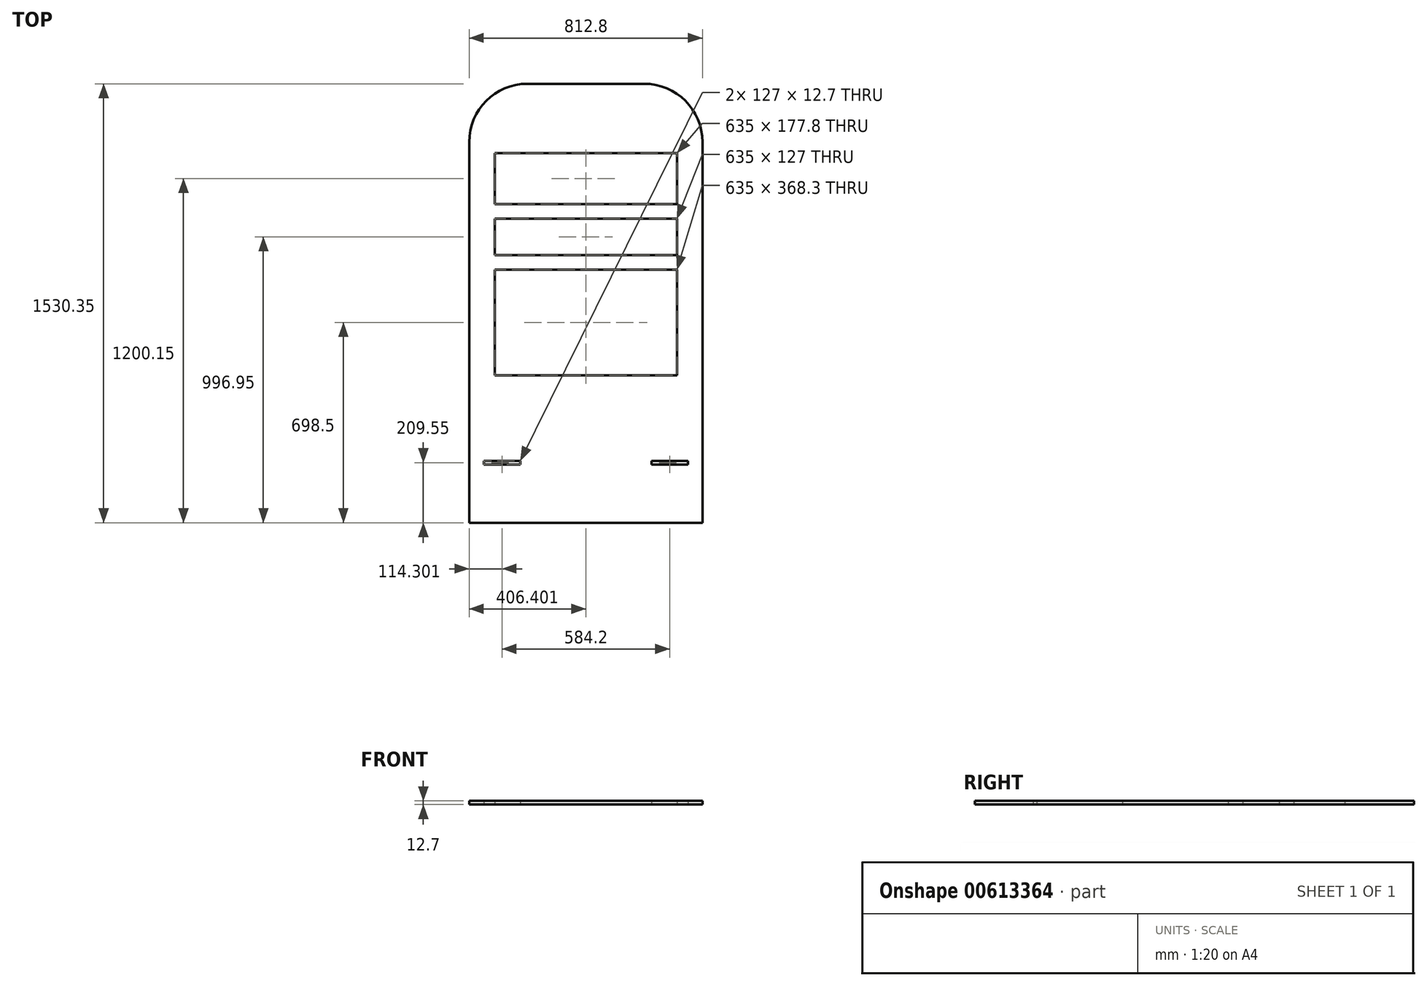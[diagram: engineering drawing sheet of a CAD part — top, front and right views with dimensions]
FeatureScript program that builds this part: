
annotation { "Feature Type Name" : "Feature", "Feature Type Description" : "" }
export const myFeature = defineFeature(function(context is Context, id is Id, definition is map)
    precondition{}
    {
        {
            var Q0;
            Q0=qCreatedBy(makeId("Top.planeOp"),FACE);
            var sketch = newSketch(context, id + "F0", { "sketchPlane" : qUnion([Q0])});
            skLineSegment(sketch, "E0.left", {"start": v(-648.04, 763.82) * mm, "end": v(-648.04, -556.98) * mm});
            skLineSegment(sketch, "E0.right", {"start": v(164.76, 763.82) * mm, "end": v(164.76, -556.98) * mm});
            skLineSegment(sketch, "E1.0", {"start": v(-559.14, -48.98) * mm, "end": v(75.86, -48.98) * mm});
            skLineSegment(sketch, "E2.0", {"start": v(-559.14, 725.72) * mm, "end": v(-559.14, 547.92) * mm});
            skLineSegment(sketch, "E3.0", {"start": v(-559.14, 725.72) * mm, "end": v(75.86, 725.72) * mm});
            skLineSegment(sketch, "E4.0", {"start": v(75.86, 725.72) * mm, "end": v(75.86, 547.92) * mm});
            skLineSegment(sketch, "E5.0", {"start": v(-559.14, 319.32) * mm, "end": v(75.86, 319.32) * mm});
            skLineSegment(sketch, "E6.trimOffspring", {"start": v(-559.14, 90.72) * mm, "end": v(-559.14, -48.98) * mm});
            skLineSegment(sketch, "E7.trimOffspring", {"start": v(75.86, 90.72) * mm, "end": v(75.86, -48.98) * mm});
            skLineSegment(sketch, "E8.trimOffspring", {"start": v(75.86, 319.32) * mm, "end": v(75.86, 141.52) * mm});
            skLineSegment(sketch, "E9.trimOffspring", {"start": v(-559.14, 319.32) * mm, "end": v(-559.14, 141.52) * mm});
            skLineSegment(sketch, "E10.trimOffspring", {"start": v(-559.14, 497.12) * mm, "end": v(-559.14, 370.12) * mm});
            skLineSegment(sketch, "E11.trimOffspring", {"start": v(75.86, 497.12) * mm, "end": v(75.86, 370.12) * mm});
            skLineSegment(sketch, "E12", {"start": v(-559.14, 370.12) * mm, "end": v(75.86, 370.12) * mm});
            skLineSegment(sketch, "E13", {"start": v(-559.14, 90.72) * mm, "end": v(-559.14, 141.52) * mm});
            skLineSegment(sketch, "E14", {"start": v(75.86, 90.72) * mm, "end": v(75.86, 141.52) * mm});
            skLineSegment(sketch, "E15", {"start": v(-559.14, 547.92) * mm, "end": v(75.86, 547.92) * mm});
            skLineSegment(sketch, "E16", {"start": v(75.86, 497.12) * mm, "end": v(-559.14, 497.12) * mm});
            skLineSegment(sketch, "E17", {"start": v(-444.84, 967.02) * mm, "end": v(-38.44, 967.02) * mm});
            skPoint(sketch, "E18.visualSharp", {"position": v(-648.04, 967.02) * mm});
            skArc(sketch, "E18.filletArc", {"start": v(-444.84, 967.02) * mm, "mid": v(-588.52, 907.5) * mm, "end": v(-648.04, 763.82) * mm});
            skPoint(sketch, "E19.visualSharp", {"position": v(164.76, 967.02) * mm});
            skArc(sketch, "E19.filletArc", {"start": v(164.76, 763.82) * mm, "mid": v(105.25, 907.5) * mm, "end": v(-38.44, 967.02) * mm});
            skLineSegment(sketch, "E20.0", {"start": v(-648.04, -563.33) * mm, "end": v(164.76, -563.33) * mm});
            skLineSegment(sketch, "E21", {"start": v(-648.04, -556.98) * mm, "end": v(-648.04, -563.33) * mm});
            skLineSegment(sketch, "E22", {"start": v(164.76, -556.98) * mm, "end": v(164.76, -563.33) * mm});
            skLineSegment(sketch, "E23.MirrorCS", {"start": v(-597.24, -360.13) * mm, "end": v(-597.24, -347.43) * mm});
            skLineSegment(sketch, "E24.MirrorCS", {"start": v(-470.24, -360.13) * mm, "end": v(-470.24, -347.43) * mm});
            skLineSegment(sketch, "E25.MirrorCS", {"start": v(113.96, -360.13) * mm, "end": v(113.96, -347.43) * mm});
            skLineSegment(sketch, "E26.MirrorCS", {"start": v(-13.04, -360.13) * mm, "end": v(-13.04, -347.43) * mm});
            skLineSegment(sketch, "E27.MirrorCS", {"start": v(-597.24, -360.13) * mm, "end": v(-470.24, -360.13) * mm});
            skLineSegment(sketch, "E28.MirrorCS", {"start": v(-13.04, -360.13) * mm, "end": v(113.96, -360.13) * mm});
            skLineSegment(sketch, "E29.MirrorCS", {"start": v(-597.24, -347.43) * mm, "end": v(-470.24, -347.43) * mm});
            skLineSegment(sketch, "E30.MirrorCS", {"start": v(-13.04, -347.43) * mm, "end": v(113.96, -347.43) * mm});
            skSolve(sketch);
        }
        {
            var Q0;
            Q0=makeQuery(id+"F0.imprint","IMPRINT",FACE,{"disambiguationData":[TD([[makeQuery(id+"F0.imprint","IMPRINT",EDGE,{"derivedFrom":sQuery(id+"F0.wireOp",EDGE,"E0.top")}),1.0]])]});
            var Q1;
            Q1=makeQuery(id+"F0.imprint","IMPRINT",FACE,{"disambiguationData":[TD([[makeQuery(id+"F0.imprint","IMPRINT",EDGE,{"derivedFrom":sQuery(id+"F0.wireOp",EDGE,"E0.left")}),1.0]])]});
            extrude(context, id + "F1", {"entities" : qUnion([Q0, Q1]), "depth" : 12.7 * mm, "offsetDistance" : 25.4 * mm});
        }
    });
